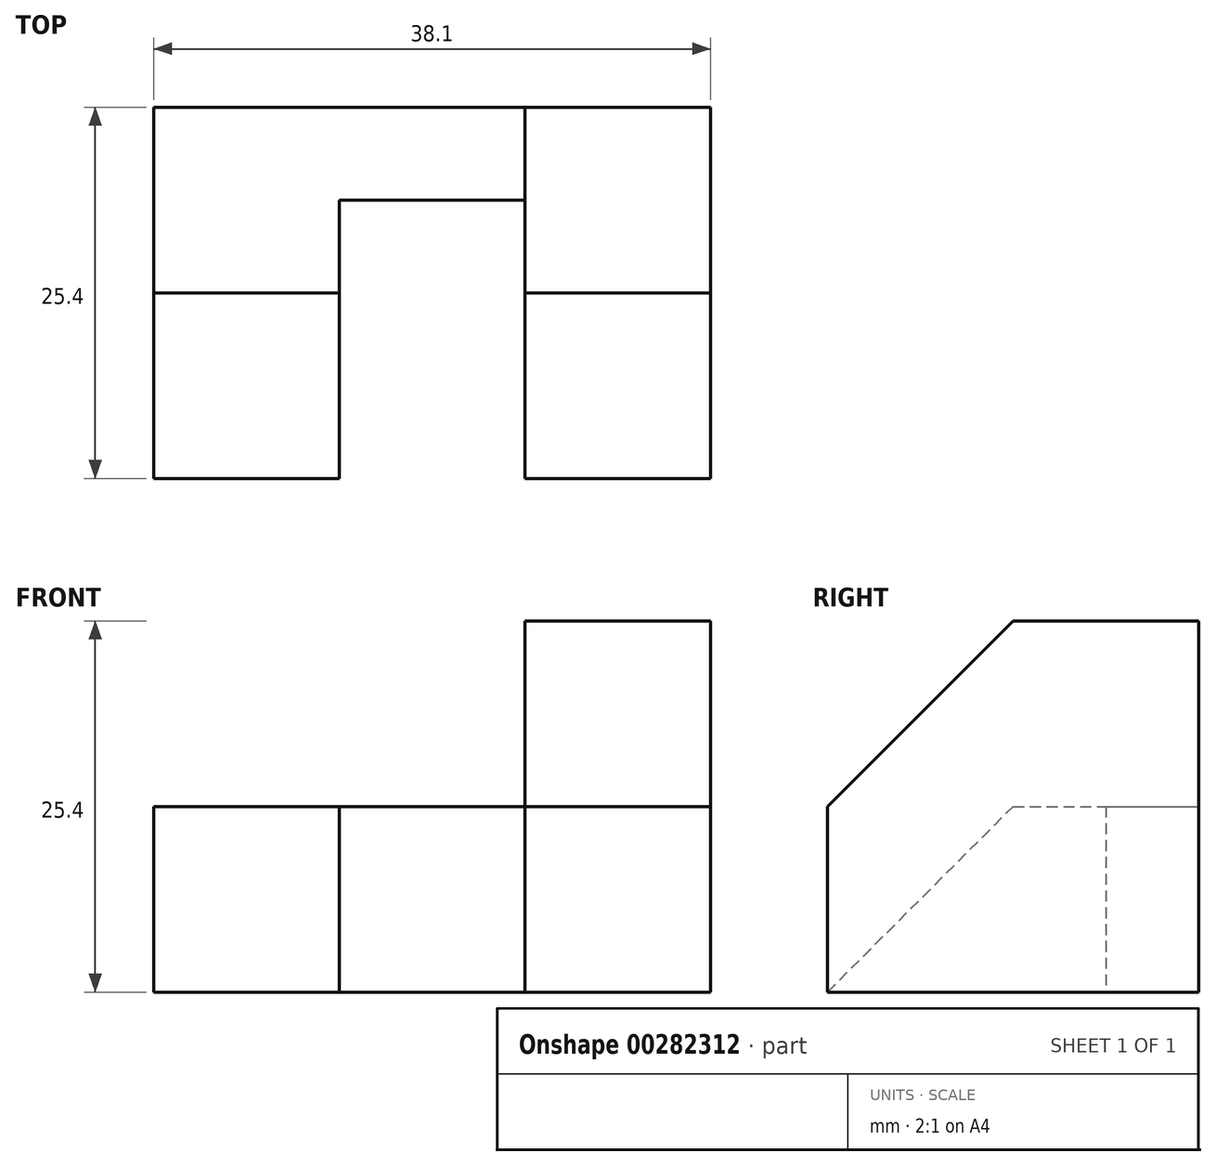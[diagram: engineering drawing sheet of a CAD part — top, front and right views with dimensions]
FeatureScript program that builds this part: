
annotation { "Feature Type Name" : "Feature", "Feature Type Description" : "" }
export const myFeature = defineFeature(function(context is Context, id is Id, definition is map)
    precondition{}
    {
        {
            var Q0;
            Q0=qCreatedBy(makeId("Right.planeOp"),FACE);
            var sketch = newSketch(context, id + "F0", { "sketchPlane" : qUnion([Q0])});
            skLineSegment(sketch, "E0", {"start": v(0, 0) * mm, "end": v(12.7, 12.7) * mm});
            skLineSegment(sketch, "E1", {"start": v(12.7, 12.7) * mm, "end": v(25.4, 12.7) * mm});
            skLineSegment(sketch, "E2", {"start": v(25.4, 12.7) * mm, "end": v(25.4, 0) * mm});
            skLineSegment(sketch, "E3", {"start": v(25.4, 0) * mm, "end": v(0, 0) * mm});
            skSolve(sketch);
        }
        {
            var Q0;
            Q0 = qSketchRegion(id + "F0", true);
            extrude(context, id + "F1", {"entities" : qUnion([Q0]), "depth" : 12.7 * mm});
        }
        {
            var Q0;
            Q0=makeQuery(id+"F1.opExtrude","CAP_FACE",FACE,{"disambiguationData":[OSD([sQuery(id+"F0.wireOp",EDGE,"E0"),sQuery(id+"F0.wireOp",EDGE,"E1"),sQuery(id+"F0.wireOp",EDGE,"E2"),sQuery(id+"F0.wireOp",EDGE,"E3")])],"isStart":false});
            var sketch = newSketch(context, id + "F2", { "sketchPlane" : qUnion([Q0])});
            skLineSegment(sketch, "E4", {"start": v(25.4, 12.7) * mm, "end": v(19.05, 12.7) * mm});
            skLineSegment(sketch, "E5", {"start": v(19.05, 12.7) * mm, "end": v(19.05, 0) * mm});
            skLineSegment(sketch, "E6", {"start": v(19.05, 0) * mm, "end": v(25.4, 0) * mm});
            skLineSegment(sketch, "E7", {"start": v(25.4, 0) * mm, "end": v(25.4, 12.7) * mm});
            skSolve(sketch);
        }
        {
            var Q0;
            Q0=makeQuery(id+"F2.imprint","IMPRINT",FACE,{"disambiguationData":[TD([[makeQuery(id+"F2.imprint","IMPRINT",EDGE,{"derivedFrom":sQuery(id+"F2.wireOp",EDGE,"E4")}),-1.0]])]});
            extrude(context, id + "F3", {"entities" : qUnion([Q0]), "operationType" : NewBodyOperationType.ADD, "depth" : 12.7 * mm});
        }
        {
            var Q0;
            Q0=makeQuery(id+"F3.opExtrude","CAP_FACE",FACE,{"disambiguationData":[OSD([sQuery(id+"F2.wireOp",EDGE,"E4"),sQuery(id+"F2.wireOp",EDGE,"E5"),sQuery(id+"F2.wireOp",EDGE,"E6"),sQuery(id+"F2.wireOp",EDGE,"E7")])],"isStart":false});
            var sketch = newSketch(context, id + "F4", { "sketchPlane" : qUnion([Q0])});
            skLineSegment(sketch, "E8", {"start": v(25.4, 0) * mm, "end": v(25.4, 25.4) * mm});
            skLineSegment(sketch, "E9", {"start": v(25.4, 25.4) * mm, "end": v(12.7, 25.4) * mm});
            skLineSegment(sketch, "E10", {"start": v(12.7, 25.4) * mm, "end": v(0, 12.7) * mm});
            skLineSegment(sketch, "E11", {"start": v(0, 12.7) * mm, "end": v(0, 0) * mm});
            skLineSegment(sketch, "E12", {"start": v(0, 0) * mm, "end": v(25.4, 0) * mm});
            skSolve(sketch);
        }
        {
            var Q0;
            Q0 = qSketchRegion(id + "F4", true);
            extrude(context, id + "F5", {"entities" : qUnion([Q0]), "operationType" : NewBodyOperationType.ADD, "depth" : 12.7 * mm});
        }
    });
